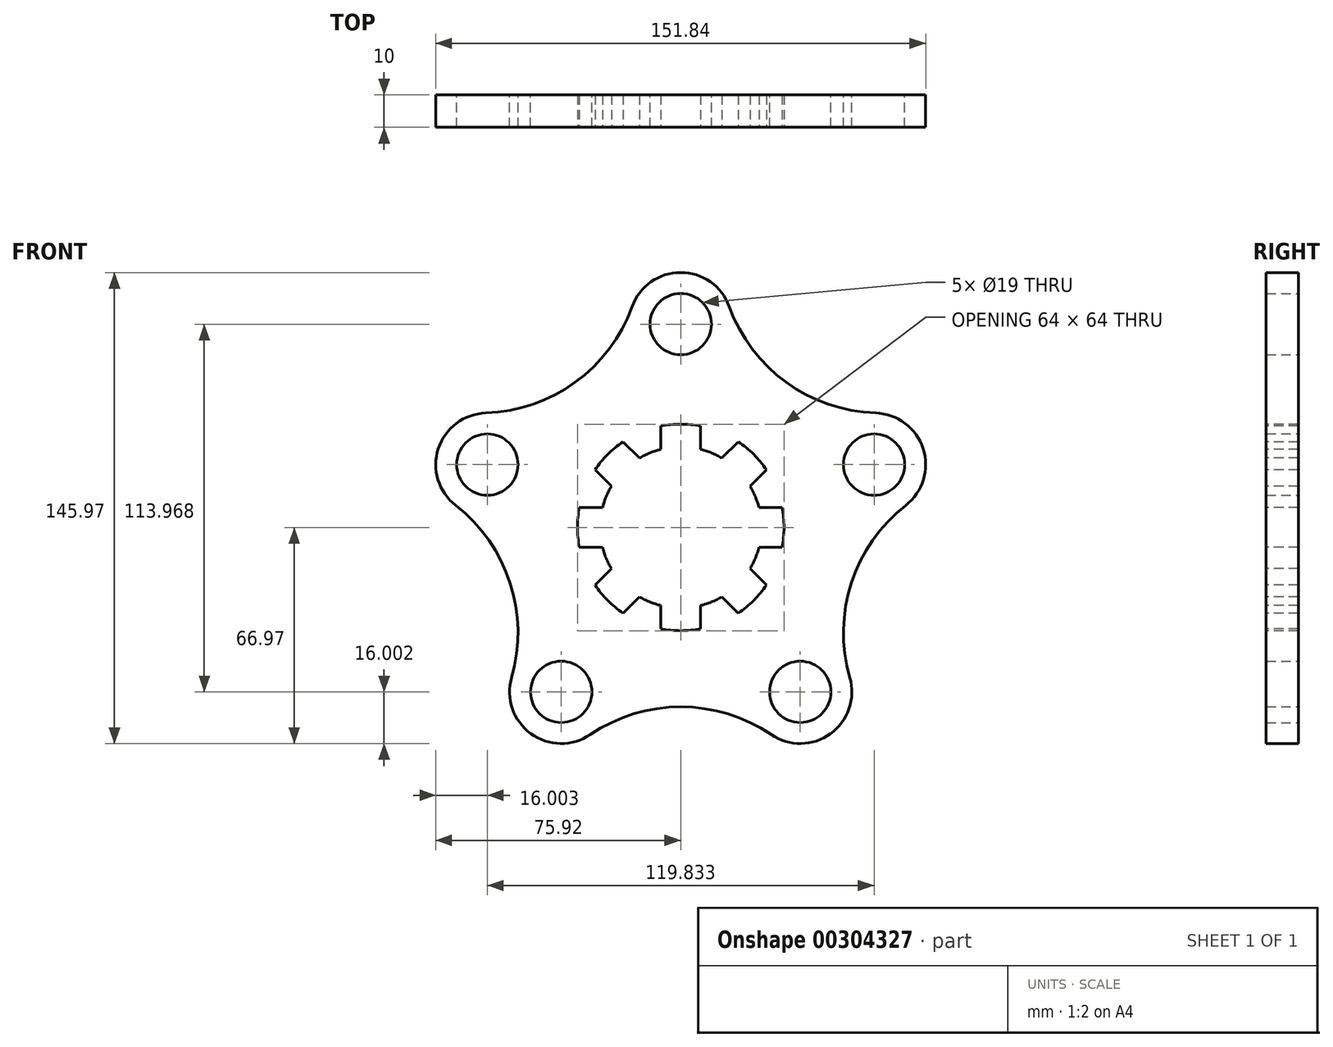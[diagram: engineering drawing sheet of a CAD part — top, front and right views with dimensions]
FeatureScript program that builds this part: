
annotation { "Feature Type Name" : "Feature", "Feature Type Description" : "" }
export const myFeature = defineFeature(function(context is Context, id is Id, definition is map)
    precondition{}
    {
        {
            var Q0;
            Q0=qCreatedBy(makeId("Front.planeOp"),FACE);
            var sketch = newSketch(context, id + "F0", { "sketchPlane" : qUnion([Q0])});
            skCircle(sketch, "E0", {"center": v(0, 0) * mm, "radius": 63 * mm, "construction": true});
            skCircle(sketch, "E1", {"center": v(0, 63) * mm, "radius": 9.5 * mm});
            skCircle(sketch, "E2", {"center": v(0, 63) * mm, "radius": 16 * mm});
            skCircle(sketch, "E3.1.0", {"center": v(-59.92, 19.47) * mm, "radius": 9.5 * mm});
            skCircle(sketch, "E3.1.1", {"center": v(-59.92, 19.47) * mm, "radius": 16 * mm});
            skCircle(sketch, "E3.2.0", {"center": v(-37.03, -50.97) * mm, "radius": 9.5 * mm});
            skCircle(sketch, "E3.2.1", {"center": v(-37.03, -50.97) * mm, "radius": 16 * mm});
            skCircle(sketch, "E3.3.0", {"center": v(37.03, -50.97) * mm, "radius": 9.5 * mm});
            skCircle(sketch, "E3.3.1", {"center": v(37.03, -50.97) * mm, "radius": 16 * mm});
            skCircle(sketch, "E3.4.0", {"center": v(59.92, 19.47) * mm, "radius": 9.5 * mm});
            skCircle(sketch, "E3.4.1", {"center": v(59.92, 19.47) * mm, "radius": 16 * mm});
            skArc(sketch, "E4", {"start": v(-60.44, 35.46) * mm, "mid": v(-32.68, 44.98) * mm, "end": v(-15.05, 68.44) * mm});
            skArc(sketch, "E5.1.0", {"start": v(-52.4, -46.52) * mm, "mid": v(-52.88, -17.18) * mm, "end": v(-69.74, 6.84) * mm});
            skArc(sketch, "E5.2.0", {"start": v(28.05, -64.21) * mm, "mid": v(0, -55.6) * mm, "end": v(-28.05, -64.21) * mm});
            skArc(sketch, "E5.3.0", {"start": v(69.74, 6.84) * mm, "mid": v(52.88, -17.18) * mm, "end": v(52.4, -46.52) * mm});
            skArc(sketch, "E5.4.0", {"start": v(15.05, 68.44) * mm, "mid": v(32.68, 44.98) * mm, "end": v(60.44, 35.46) * mm});
            skSolve(sketch);
        }
        {
            var Q0;
            Q0 = qSketchRegion(id + "F0", true);
            extrude(context, id + "F1", {"entities" : qUnion([Q0]), "endBound" : BoundingType.SYMMETRIC, "depth" : 10 * mm});
        }
        {
            var Q0;
            Q0=makeQuery(id+"F1.opExtrude","CAP_FACE",FACE,{"disambiguationData":[OSD([sQuery(id+"F0.wireOp",EDGE,"E1"),sQuery(id+"F0.wireOp",EDGE,"E2"),sQuery(id+"F0.wireOp",EDGE,"E3.1.0"),sQuery(id+"F0.wireOp",EDGE,"E3.1.1"),sQuery(id+"F0.wireOp",EDGE,"E3.2.0"),sQuery(id+"F0.wireOp",EDGE,"E3.2.1"),sQuery(id+"F0.wireOp",EDGE,"E3.3.0"),sQuery(id+"F0.wireOp",EDGE,"E3.3.1"),sQuery(id+"F0.wireOp",EDGE,"E3.4.0"),sQuery(id+"F0.wireOp",EDGE,"E3.4.1"),sQuery(id+"F0.wireOp",EDGE,"E4"),sQuery(id+"F0.wireOp",EDGE,"E5.1.0"),sQuery(id+"F0.wireOp",EDGE,"E5.2.0"),sQuery(id+"F0.wireOp",EDGE,"E5.3.0"),sQuery(id+"F0.wireOp",EDGE,"E5.4.0")])],"isStart":false});
            var sketch = newSketch(context, id + "F2", { "sketchPlane" : qUnion([Q0])});
            skArc(sketch, "E6", {"start": v(26.55, 17.86) * mm, "mid": v(22.63, 22.63) * mm, "end": v(17.86, 26.55) * mm});
            skArc(sketch, "E7", {"start": v(-6.15, 24.23) * mm, "mid": v(-9.57, 23.1) * mm, "end": v(-12.79, 21.48) * mm});
            skLineSegment(sketch, "E8.0", {"start": v(-6.15, 31.4) * mm, "end": v(-6.15, 24.23) * mm});
            skLineSegment(sketch, "E9.0", {"start": v(6.15, 31.4) * mm, "end": v(6.15, 24.23) * mm});
            skLineSegment(sketch, "E10.1.0", {"start": v(-26.55, 17.86) * mm, "end": v(-21.48, 12.79) * mm});
            skLineSegment(sketch, "E10.1.1", {"start": v(-17.86, 26.55) * mm, "end": v(-12.79, 21.48) * mm});
            skLineSegment(sketch, "E10.2.0", {"start": v(-31.4, -6.15) * mm, "end": v(-24.23, -6.15) * mm});
            skLineSegment(sketch, "E10.2.1", {"start": v(-31.4, 6.15) * mm, "end": v(-24.23, 6.15) * mm});
            skLineSegment(sketch, "E10.3.0", {"start": v(-17.86, -26.55) * mm, "end": v(-12.79, -21.48) * mm});
            skLineSegment(sketch, "E10.3.1", {"start": v(-26.55, -17.86) * mm, "end": v(-21.48, -12.79) * mm});
            skLineSegment(sketch, "E10.4.0", {"start": v(6.15, -31.4) * mm, "end": v(6.15, -24.23) * mm});
            skLineSegment(sketch, "E10.4.1", {"start": v(-6.15, -31.4) * mm, "end": v(-6.15, -24.23) * mm});
            skLineSegment(sketch, "E10.5.0", {"start": v(26.55, -17.86) * mm, "end": v(21.48, -12.79) * mm});
            skLineSegment(sketch, "E10.5.1", {"start": v(17.86, -26.55) * mm, "end": v(12.79, -21.48) * mm});
            skLineSegment(sketch, "E10.6.0", {"start": v(31.4, 6.15) * mm, "end": v(24.23, 6.15) * mm});
            skLineSegment(sketch, "E10.6.1", {"start": v(31.4, -6.15) * mm, "end": v(24.23, -6.15) * mm});
            skLineSegment(sketch, "E10.7.0", {"start": v(17.86, 26.55) * mm, "end": v(12.79, 21.48) * mm});
            skLineSegment(sketch, "E10.7.1", {"start": v(26.55, 17.86) * mm, "end": v(21.48, 12.79) * mm});
            skArc(sketch, "E11.trimOffspring", {"start": v(12.79, 21.48) * mm, "mid": v(9.57, 23.1) * mm, "end": v(6.15, 24.23) * mm});
            skArc(sketch, "E12.trimOffspring", {"start": v(6.15, 31.4) * mm, "mid": v(0, 32) * mm, "end": v(-6.15, 31.4) * mm});
            skArc(sketch, "E13.trimOffspring", {"start": v(-26.55, -17.86) * mm, "mid": v(-22.63, -22.63) * mm, "end": v(-17.86, -26.55) * mm});
            skArc(sketch, "E14.trimOffspring", {"start": v(-17.86, 26.55) * mm, "mid": v(-22.63, 22.63) * mm, "end": v(-26.55, 17.86) * mm});
            skArc(sketch, "E15.trimOffspring", {"start": v(-31.4, 6.15) * mm, "mid": v(-32, 0) * mm, "end": v(-31.4, -6.15) * mm});
            skArc(sketch, "E16.trimOffspring", {"start": v(-21.48, 12.79) * mm, "mid": v(-23.1, 9.57) * mm, "end": v(-24.23, 6.15) * mm});
            skArc(sketch, "E17.trimOffspring", {"start": v(24.23, 6.15) * mm, "mid": v(23.1, 9.57) * mm, "end": v(21.48, 12.79) * mm});
            skArc(sketch, "E18.trimOffspring", {"start": v(-24.23, -6.15) * mm, "mid": v(-23.1, -9.57) * mm, "end": v(-21.48, -12.79) * mm});
            skArc(sketch, "E19.trimOffspring", {"start": v(6.15, -24.23) * mm, "mid": v(9.57, -23.1) * mm, "end": v(12.79, -21.48) * mm});
            skArc(sketch, "E20.trimOffspring", {"start": v(21.48, -12.79) * mm, "mid": v(23.1, -9.57) * mm, "end": v(24.23, -6.15) * mm});
            skArc(sketch, "E21.trimOffspring", {"start": v(-12.79, -21.48) * mm, "mid": v(-9.57, -23.1) * mm, "end": v(-6.15, -24.23) * mm});
            skArc(sketch, "E22.trimOffspring", {"start": v(17.86, -26.55) * mm, "mid": v(22.63, -22.63) * mm, "end": v(26.55, -17.86) * mm});
            skArc(sketch, "E23.trimOffspring", {"start": v(-6.15, -31.4) * mm, "mid": v(0, -32) * mm, "end": v(6.15, -31.4) * mm});
            skArc(sketch, "E24.trimOffspring", {"start": v(31.4, -6.15) * mm, "mid": v(32, 0) * mm, "end": v(31.4, 6.15) * mm});
            skPoint(sketch, "E25.start.orphan", {"position": v(0, 32) * mm});
            skSolve(sketch);
        }
        {
            var Q0;
            Q0 = qSketchRegion(id + "F2", true);
            extrude(context, id + "F3", {"entities" : qUnion([Q0]), "operationType" : NewBodyOperationType.REMOVE, "oppositeDirection" : true, "depth" : 25 * mm});
        }
    });
